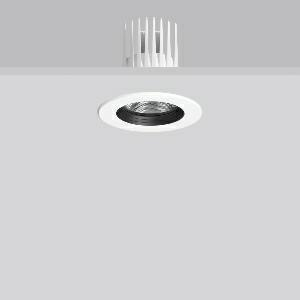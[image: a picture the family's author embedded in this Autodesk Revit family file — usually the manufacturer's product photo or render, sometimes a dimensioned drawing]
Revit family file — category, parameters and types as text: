
# Revit family: heledon_mini_e_901748_002_2_bf43
name_source: partatom
category: Lighting Fixtures
units: mm (PartAtom-declared; Revit-internal decimal feet)

## family parameters
Cut with Voids When Loaded = No
Host = Face
Light Source = No
Part Type = Normal
Room Calculation Point = No
Round Connector Dimension = Use Diameter
Shared = No

## types (1)
- HELEDON mini E (1 x LED Modul 927, 3400 lm, 2700)
    Apparent Load = 29 VA
    Approval mark = CE
    CIE Flux Codes = 100 100 100 100 100
    Color Rendering = 92
    Color Temperature = 2700
    Default Elevation = 1800 mm
    Description = Series: HELEDON mini
Round recessed downlight. Housing: die-cast aluminium, powder-coated. Black plastic ring and recessed LED to prevent glare from the side. Optical assembly with reflector made of MIRO-Silver with 98% total light reflection for outstanding efficiency - can be changed without tools. Best colour rendering index Ra>90. Suitable for Recessed ceiling mounting. Installation without tools thanks to spring fastening system. Including separate LED converter with connecting cable 600 mm.High quality converter without flickering and stroboscopic effect. Through-wiring box (5 pole) available as accessory. The following accessories can be mounted without use of tools: interchangeable lenses, decorative glasses, honeycomb louvre, clear and frosted diffusers, white interchangeable plastic ring. 
Colour: traffic white, matt (RAL 9016)
Diameter: 124 mm
Height: 3 mm
Cut-out diameter: 114 mm
Recess height: 170 mm
Luminaire: recess height: 120 mm
Lamp: LED
Socket: without socket
Colour temperature: 2700K
Colour rendering index (CRI): 92
System power: 29 W
Rated luminous flux: 3400 lm
Luminous efficiency: 117 lm/W
Control gear: Regulated power supply
Protection class: II
Type of protection: IP 20
    Height = 0 mm  [stored 0 ft]
    Lamp = 1 x LED Modul 927
    Lamp Light Flux = 3400 lm
    Lamp count = 1
    Length = 124 mm  [stored 0.406824 ft]
    Lifetime = 50000 h
    Luminous efficacy = 117 lm/W
    Manufacturer = RZB
    ModVariant = No
    Model = 901748.002.2
    Mounting Place = Ceiling
    Mounting Type = Recessed
    Number of Poles = 1
    OnlyDefault = Yes
    Power Factor = 1
    Product Name = HELEDON mini E
    Product group = Recessed downlights
    ProductGroupID = 402
    Protection Class = Protection class II
    Protection Degree = IP 20
    RLX_Detail_Level = 1
    RLX_Emergency_Light_Flux = 0 lm
    RLX_Emergency_Type = 0
    RLX_Emergency_Type_DB = No
    RlxData = <blob elided: 125805 chars, md5=f6135fe4>
    Socket = socket
    Standby Power = 0 W
    System Light Flux = 3400 lm
    System Power = 29 W
    Type Comments = Product without accessories
    Type Image = 901657.002.jpg
    URL = http://relux.com
    VarID = ---
    Voltage = 230 V
    Voltage Range = 220-240 V
    Weight = 0.00 kg
    Width = 0 mm  [stored 0 ft]

note: [stored X ft] marks values corroborated as IEEE doubles in the binary element streams (Revit-internal decimal feet)

## geometry (parser evidence)
native form markers: Blend x4, Sweep x12
no freeform markers — native parametric forms only
